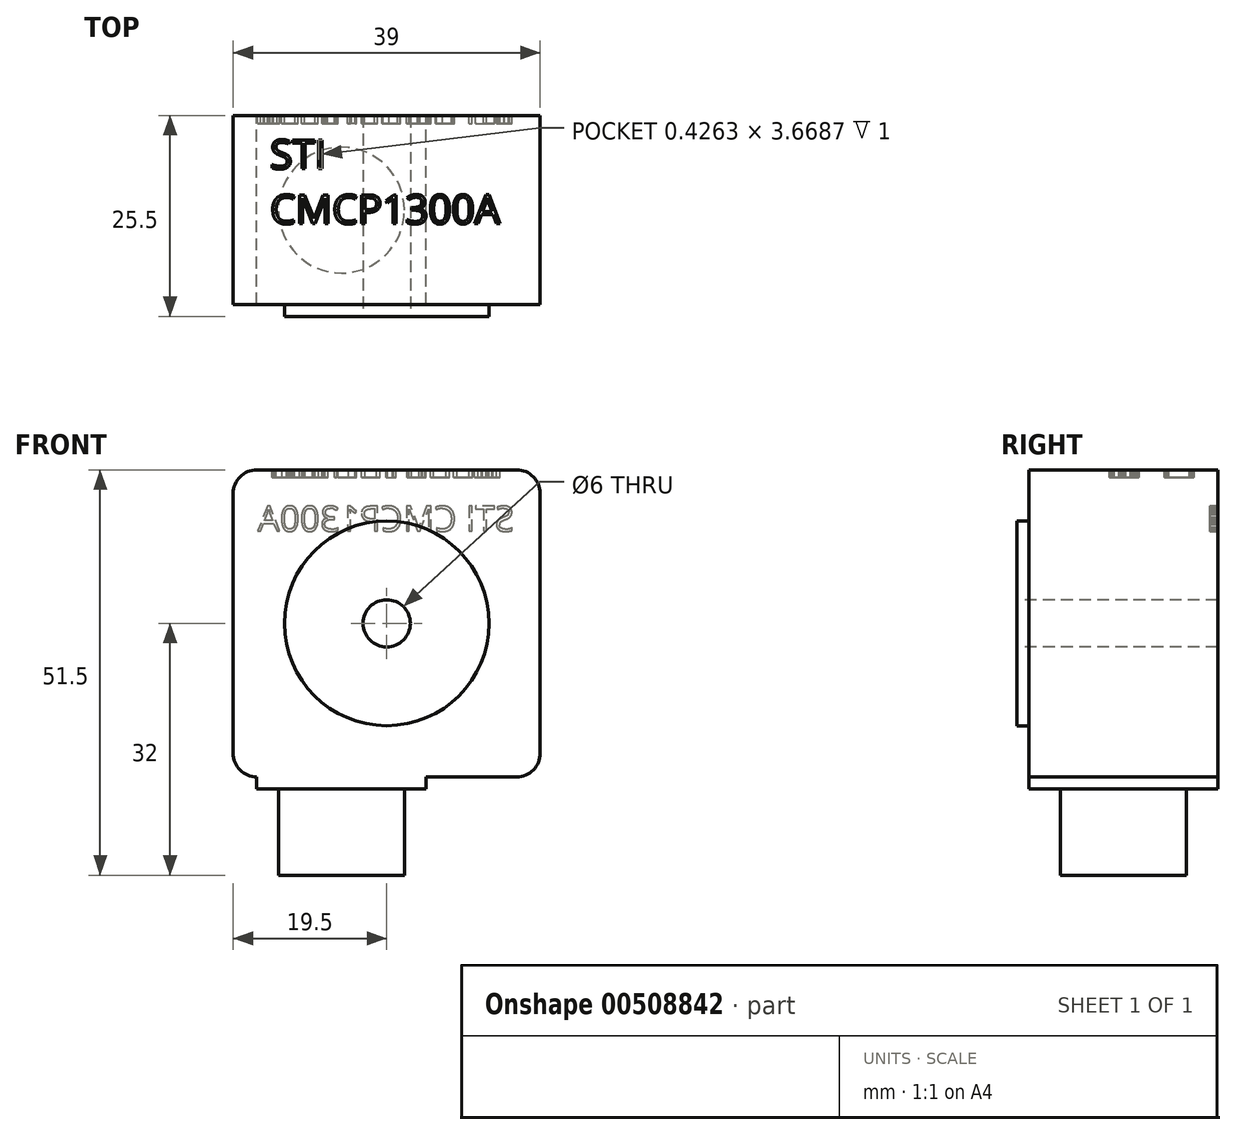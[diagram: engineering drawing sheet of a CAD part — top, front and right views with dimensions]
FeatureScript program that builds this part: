
annotation { "Feature Type Name" : "Feature", "Feature Type Description" : "" }
export const myFeature = defineFeature(function(context is Context, id is Id, definition is map)
    precondition{}
    {
        {
            var Q0;
            Q0=qCreatedBy(makeId("Front.planeOp"),FACE);
            var sketch = newSketch(context, id + "F0", { "sketchPlane" : qUnion([Q0])});
            skLineSegment(sketch, "E0.bottom", {"start": v(0, 0) * mm, "end": v(39, 0) * mm});
            skLineSegment(sketch, "E0.top", {"start": v(0, 39) * mm, "end": v(39, 39) * mm});
            skLineSegment(sketch, "E0.left", {"start": v(0, 0) * mm, "end": v(0, 39) * mm});
            skLineSegment(sketch, "E0.right", {"start": v(39, 0) * mm, "end": v(39, 39) * mm});
            skSolve(sketch);
        }
        {
            var Q0;
            Q0 = qSketchRegion(id + "F0", true);
            extrude(context, id + "F1", {"entities" : qUnion([Q0]), "depth" : 24 * mm});
        }
        {
            var Q0;
            Q0=makeQuery(id+"F1.opExtrude","SWEPT_EDGE",EDGE,{"disambiguationData":[OSD([sQuery(id+"F0.wireOp",EDGE,"E0.top"),sQuery(id+"F0.wireOp",EDGE,"E0.left")])]});
            var Q1;
            Q1=makeQuery(id+"F1.opExtrude","SWEPT_EDGE",EDGE,{"disambiguationData":[OSD([sQuery(id+"F0.wireOp",EDGE,"E0.top"),sQuery(id+"F0.wireOp",EDGE,"E0.right")])]});
            var Q2;
            Q2=makeQuery(id+"F1.opExtrude","SWEPT_EDGE",EDGE,{"disambiguationData":[OSD([sQuery(id+"F0.wireOp",EDGE,"E0.bottom"),sQuery(id+"F0.wireOp",EDGE,"E0.right")])]});
            var Q3;
            Q3=makeQuery(id+"F1.opExtrude","SWEPT_EDGE",EDGE,{"disambiguationData":[OSD([sQuery(id+"F0.wireOp",EDGE,"E0.bottom"),sQuery(id+"F0.wireOp",EDGE,"E0.left")])]});
            fillet(context, id + "F2", {"entities" : qUnion([Q0, Q1, Q2, Q3]), "radius" : 3 * mm, "tangentPropagation" : true, "allowEdgeOverflow" : false});
        }
        {
            var Q0;
            Q0=makeQuery(id+"F1.opExtrude","CAP_FACE",FACE,{"disambiguationData":[OSD([sQuery(id+"F0.wireOp",EDGE,"E0.bottom"),sQuery(id+"F0.wireOp",EDGE,"E0.top"),sQuery(id+"F0.wireOp",EDGE,"E0.left"),sQuery(id+"F0.wireOp",EDGE,"E0.right")])],"isStart":false});
            var sketch = newSketch(context, id + "F3", { "sketchPlane" : qUnion([Q0])});
            skCircle(sketch, "E1", {"center": v(19.5, 19.5) * mm, "radius": 13 * mm});
            skSolve(sketch);
        }
        {
            var Q0;
            Q0 = qSketchRegion(id + "F3", true);
            extrude(context, id + "F4", {"entities" : qUnion([Q0]), "operationType" : NewBodyOperationType.ADD, "depth" : 1.5 * mm});
        }
        {
            var Q0;
            Q0=makeQuery(id+"F4.opExtrude","CAP_FACE",FACE,{"disambiguationData":[OSD([sQuery(id+"F3.wireOp",EDGE,"E1")])],"isStart":false});
            var sketch = newSketch(context, id + "F5", { "sketchPlane" : qUnion([Q0])});
            skCircle(sketch, "E2", {"center": v(19.5, 19.5) * mm, "radius": 3 * mm});
            skSolve(sketch);
        }
        {
            var Q0;
            Q0 = qSketchRegion(id + "F5", true);
            extrude(context, id + "F6", {"entities" : qUnion([Q0]), "operationType" : NewBodyOperationType.REMOVE, "endBound" : BoundingType.THROUGH_ALL, "oppositeDirection" : true, "depth" : 25 * mm});
        }
        {
            var Q0;
            Q0=makeQuery(id+"F1.opExtrude","SWEPT_FACE",FACE,{"disambiguationData":[OSD([sQuery(id+"F0.wireOp",EDGE,"E0.bottom")])]});
            var sketch = newSketch(context, id + "F7", { "sketchPlane" : qUnion([Q0])});
            skPoint(sketch, "E3.orphan", {"position": v(36, 12) * mm});
            skLineSegment(sketch, "E4", {"start": v(3, 0) * mm, "end": v(24.5, 0) * mm});
            skLineSegment(sketch, "E5", {"start": v(3, 0) * mm, "end": v(3, 24) * mm});
            skLineSegment(sketch, "E6", {"start": v(3, 24) * mm, "end": v(24.5, 24) * mm});
            skLineSegment(sketch, "E7", {"start": v(24.5, 24) * mm, "end": v(24.5, 0) * mm});
            skSolve(sketch);
        }
        {
            var Q0;
            Q0 = qSketchRegion(id + "F7", true);
            extrude(context, id + "F8", {"entities" : qUnion([Q0]), "operationType" : NewBodyOperationType.ADD, "depth" : 1.5 * mm});
        }
        {
            var Q0;
            Q0=makeQuery(id+"F8.opExtrude","CAP_FACE",FACE,{"disambiguationData":[OSD([sQuery(id+"F7.wireOp",EDGE,"E4"),sQuery(id+"F7.wireOp",EDGE,"E5"),sQuery(id+"F7.wireOp",EDGE,"E6"),sQuery(id+"F7.wireOp",EDGE,"E7")])],"isStart":false});
            var sketch = newSketch(context, id + "F9", { "sketchPlane" : qUnion([Q0])});
            skCircle(sketch, "E8", {"center": v(13.75, 12) * mm, "radius": 8 * mm});
            skSolve(sketch);
        }
        {
            var Q0;
            Q0 = qSketchRegion(id + "F9", true);
            extrude(context, id + "F10", {"entities" : qUnion([Q0]), "operationType" : NewBodyOperationType.ADD, "depth" : 11 * mm});
        }
        {
            var Q0;
            Q0=makeQuery(id+"F8.boolean.opBoolean","MERGE",FACE,{"derivedFrom":[makeQuery(id+"F1.opExtrude","CAP_FACE",FACE,{"disambiguationData":[OSD([sQuery(id+"F0.wireOp",EDGE,"E0.bottom"),sQuery(id+"F0.wireOp",EDGE,"E0.top"),sQuery(id+"F0.wireOp",EDGE,"E0.left"),sQuery(id+"F0.wireOp",EDGE,"E0.right")])],"isStart":true}),makeQuery(id+"F8.opExtrude","SWEPT_FACE",FACE,{"disambiguationData":[OSD([sQuery(id+"F7.wireOp",EDGE,"E4")])]})]});
            var sketch = newSketch(context, id + "F11", { "sketchPlane" : qUnion([Q0])});
            skText(sketch, "E9", { "text": "STI CMCP1300A", "fontName": "OpenSans-Regular.ttf"});
            const initialGuessF11  = {"E9": [-0.03567, 0.03121, 1, 0, 0.0032]};
            skSetInitialGuess(sketch, initialGuessF11);
            skSolve(sketch);
        }
        {
            var Q0;
            Q0 = qSketchRegion(id + "F11", true);
            extrude(context, id + "F12", {"entities" : qUnion([Q0]), "operationType" : NewBodyOperationType.REMOVE, "oppositeDirection" : true, "depth" : 1 * mm});
        }
        {
            var Q0;
            Q0=makeQuery(id+"F1.opExtrude","SWEPT_FACE",FACE,{"disambiguationData":[OSD([sQuery(id+"F0.wireOp",EDGE,"E0.top")])]});
            var sketch = newSketch(context, id + "F13", { "sketchPlane" : qUnion([Q0])});
            skText(sketch, "E10", { "text": "STI\nCMCP1300A", "fontName": "OpenSans-Regular.ttf"});
            const initialGuessF13  = {"E10": [0.0047, -0.00675, 1, 0, 0.0037]};
            skSetInitialGuess(sketch, initialGuessF13);
            skSolve(sketch);
        }
        {
            var Q0;
            Q0 = qSketchRegion(id + "F13", true);
            extrude(context, id + "F14", {"entities" : qUnion([Q0]), "operationType" : NewBodyOperationType.REMOVE, "oppositeDirection" : true, "depth" : 1 * mm});
        }
    });
